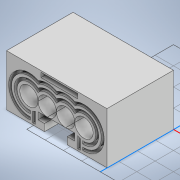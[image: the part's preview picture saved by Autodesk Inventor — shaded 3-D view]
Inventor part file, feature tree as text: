
AUTODESK INVENTOR PART (.ipt)
format: ipt  version: 2020.3 (Build 243373010, 373A)  size: 236,544 bytes
history: native  units: mm
features: extrude x1, sketch x1
ambient origin geometry x8: Origin, YZ Plane, XZ Plane, XY Plane, X Axis, Y Axis, Z Axis, Center Point
bodies: Solid1 (feature_tree)
feature tree (2):
  extrude  "Extrusion1"  Depth=3.0mm
  sketch  "Sketch2"  dims[d10=20.0mm d11=20.0mm d12=20.0mm d13=20.0mm d14=20.0mm d15=20.0mm d16=20.0mm d17=5.0mm d18=40.0mm d19=72.5mm d20=0.0mm d21=7.5mm d22=40.0mm d23=3.0mm d24=3.0mm d25=3.0mm d26=3.0mm d27=1.693376mm d28=1.693376mm d29=3.0mm d30=3.0mm d31=3.0mm d32=3.0mm d33=3.0mm d34=2.0mm d35=2.5mm d36=3.0mm d37=3.0mm d38=3.0mm d39=2.0mm d40=2.5mm d41=3.0mm d42=3.0mm d43=3.0mm d44=3.0mm d45=3.0mm d46=3.0mm d47=3.0mm d48=3.0mm]
